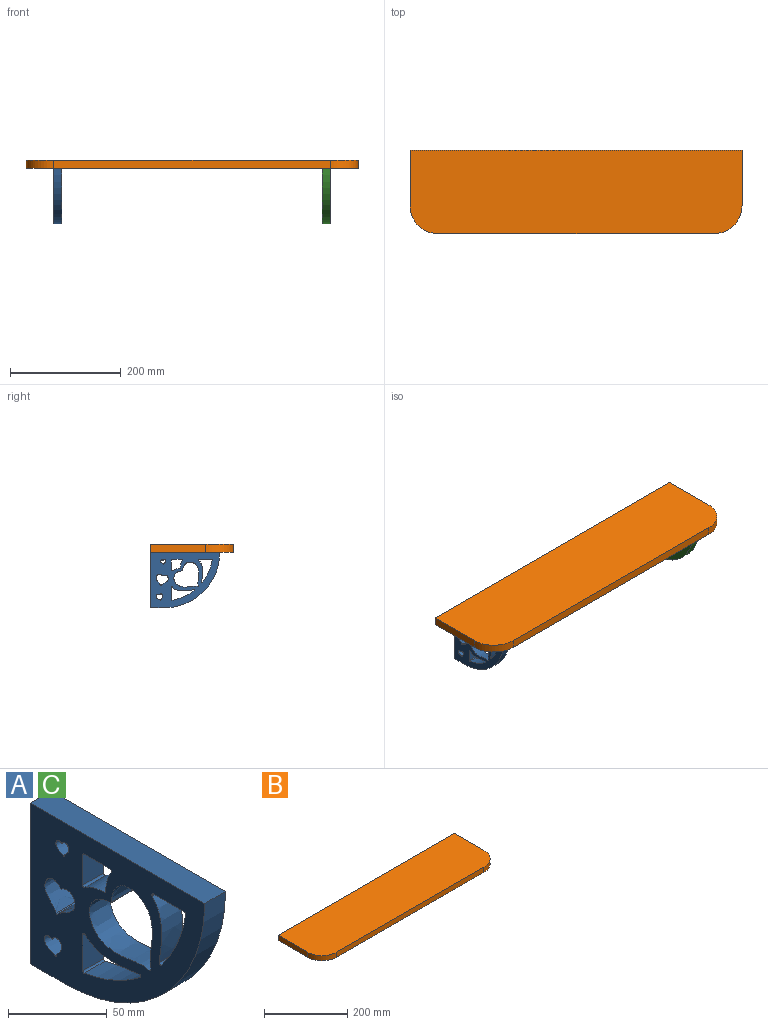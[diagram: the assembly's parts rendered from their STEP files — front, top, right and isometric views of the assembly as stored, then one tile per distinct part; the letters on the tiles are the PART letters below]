
ASSEMBLY  parts=3 mates=1
PART A: 42 faces, bbox 15x125x100 mm
  f0: plane 125x100mm, normal (-1,0,0), area 7043.4mm2, adj f2,f3,f4,f5,f6,f7,f8,f9
  f1: plane 125x100mm, normal (1,0,0), area 7043.4mm2, adj f2,f3,f4,f5,f6,f7,f8,f9
  f2: extruded ~38.71x15mm, area 607.3mm2, adj f0,f1,f27,f31
  f3: extruded ~38.71x15mm, area 607.3mm2, adj f0,f1,f26,f30
  f4: extruded ~15x13.96mm, area 221.1mm2, adj f0,f1,f32,f35
  f5: extruded ~15x13.96mm, area 221.1mm2, adj f0,f1,f29,f35
  f6: extruded ~42.79x29.15mm, area 1109mm2, adj f0,f1,f33,f34
  f7: extruded ~42.79x29.15mm, area 1109mm2, adj f0,f1,f33,f34
  f8: cylinder r=87.5mm len=40mm, axis (1,0,0), area 660.8mm2, adj f0,f1,f24,f27
  f9: plane 22.36x15mm, normal (0,0,-1), area 335.4mm2, adj f0,f1,f24,f31
  f10: plane 18.67x15mm, normal (0,0,-1), area 280.1mm2, adj f0,f1,f28,f32
  f11: plane 18.67x15mm, normal (0,-1,0), area 280.1mm2, adj f0,f1,f28,f29
  f12: plane 22.36x15mm, normal (0,-1,0), area 335.4mm2, adj f0,f1,f25,f30
  f13: cylinder r=87.5mm len=40mm, axis (1,0,0), area 660.8mm2, adj f0,f1,f25,f26
  f14: plane 125x15mm, normal (0,0,1), area 1875mm2, adj f0,f1,f15,f17
  f15: cylinder r=100mm len=100mm, axis (1,0,0), area 2356.2mm2, adj f0,f1,f14,f16
  f16: plane 25x15mm, normal (0,0,-1), area 375mm2, adj f0,f1,f15,f17
  f17: plane 100x15mm, normal (0,1,0), area 1500mm2, adj f0,f1,f14,f16
  f18: extruded ~18.38x15mm, area 483mm2, adj f0,f1,f40,f41
  f19: extruded ~20.03x15mm, area 483mm2, adj f0,f1,f40,f41
  f20: extruded ~15x7.63mm, area 197.9mm2, adj f0,f1,f38,f39
  f21: extruded ~15x8.26mm, area 197.9mm2, adj f0,f1,f38,f39
  f22: extruded ~15x9.94mm, area 268.9mm2, adj f0,f1,f36,f37
  f23: extruded ~15x11.26mm, area 268.9mm2, adj f0,f1,f36,f37
  f24: cylinder r=1mm len=15mm, axis (1,0,0), area 25.9mm2, adj f0,f1,f8,f9
  f25: cylinder r=1mm len=15mm, axis (1,0,0), area 25.9mm2, adj f0,f1,f12,f13
  f26: cylinder r=1mm len=15mm, axis (1,0,0), area 39.4mm2, adj f0,f1,f3,f13
  f27: cylinder r=1mm len=15mm, axis (1,0,0), area 39.4mm2, adj f0,f1,f2,f8
  f28: cylinder r=1mm len=15mm, axis (1,0,0), area 23.6mm2, adj f0,f1,f10,f11
  f29: cylinder r=1mm len=15mm, axis (1,0,0), area 32.9mm2, adj f0,f1,f5,f11
  f30: cylinder r=1mm len=15mm, axis (1,0,0), area 35mm2, adj f0,f1,f3,f12
  f31: cylinder r=1mm len=15mm, axis (1,0,0), area 35mm2, adj f0,f1,f2,f9
  f32: cylinder r=1mm len=15mm, axis (1,0,0), area 32.9mm2, adj f0,f1,f4,f10
  f33: cylinder r=1mm len=15mm, axis (1,0,0), area 29.1mm2, adj f0,f1,f6,f7
  f34: cylinder r=1mm len=15mm, axis (1,0,0), area 23mm2, adj f0,f1,f6,f7
  f35: cylinder r=1mm len=15mm, axis (1,0,0), area 23.3mm2, adj f0,f1,f4,f5
  f36: cylinder r=0.5mm len=15mm, axis (1,0,0), area 11mm2, adj f0,f1,f22,f23
  f37: cylinder r=0.5mm len=15mm, axis (1,0,0), area 13.9mm2, adj f0,f1,f22,f23
  f38: cylinder r=0.5mm len=15mm, axis (1,0,0), area 13.5mm2, adj f0,f1,f20,f21
  f39: cylinder r=0.5mm len=15mm, axis (1,0,0), area 10.7mm2, adj f0,f1,f20,f21
  f40: cylinder r=0.5mm len=15mm, axis (1,0,0), area 11.4mm2, adj f0,f1,f18,f19
  f41: cylinder r=0.5mm len=15mm, axis (1,0,0), area 14.5mm2, adj f0,f1,f18,f19
PART B: 8 faces, bbox 600x150x15 mm
  f0: plane 500x15mm, normal (0,-1,0), area 7500mm2, adj f4,f5,f6,f7
  f1: plane 100x15mm, normal (1,0,0), area 1500mm2, adj f2,f4,f5,f6
  f2: plane 600x15mm, normal (0,1,0), area 9000mm2, adj f1,f3,f4,f5
  f3: plane 100x15mm, normal (-1,0,0), area 1500mm2, adj f2,f4,f5,f7
  f4: plane 600x150mm, normal (0,0,1), area 88927mm2, adj f0,f1,f2,f3,f6,f7
  f5: plane 600x150mm, normal (0,0,-1), area 88927mm2, adj f0,f1,f2,f3,f6,f7
  f6: cylinder r=50mm len=50mm, axis (0,0,1), area 1178.1mm2, adj f0,f1,f4,f5
  f7: cylinder r=50mm len=50mm, axis (0,0,-1), area 1178.1mm2, adj f0,f3,f4,f5
PART C: same geometry as A
PLACE A t=(-236.11,-80,660.81)mm
PLACE B t=(-1.11,-80,710.81)mm
PLACE C t=(248.89,-80,660.81)mm
MATE planar A.f14 <-> B.f5  axis (0,0,1) through (-243.61,-67.5,710.81)mm
